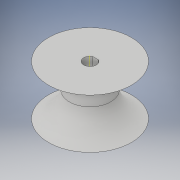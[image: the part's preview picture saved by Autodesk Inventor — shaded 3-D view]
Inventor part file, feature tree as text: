
AUTODESK INVENTOR PART (.ipt)
format: ipt  version: 2019 (Build 230136000, 136)  size: 156,672 bytes
history: native  units: in
note: dims shown in document units (in); Inventor stores cm internally (conversion verified against a paired STEP export)
features: sketch x2, revolve x1, extrude x1, mirror x1
ambient origin geometry x8: Origin, YZ Plane, XZ Plane, XY Plane, X Axis, Y Axis, Z Axis, Center Point
bodies: Body1 (feature_tree)
feature tree (5):
  revolve  "Revolution1"  [1 undecoded]
  extrude  "Extrusion1"  TaperAngle=90.0deg  [1 undecoded]
  mirror  "Mirror2"
  sketch  "Sketch4"  dims[d18=0.375in d19=0.45in]
  sketch  "Sketch5"  dims[d20=0.75in d21=90.0deg d22=0.23in d23=0.101in d24=1.0in d25=0.0in]
note: 2 required parameter values undecoded (feature->parameter linkage not recoverable at this tier; creation-order binding heuristic only, values carry confidence <= 0.55)